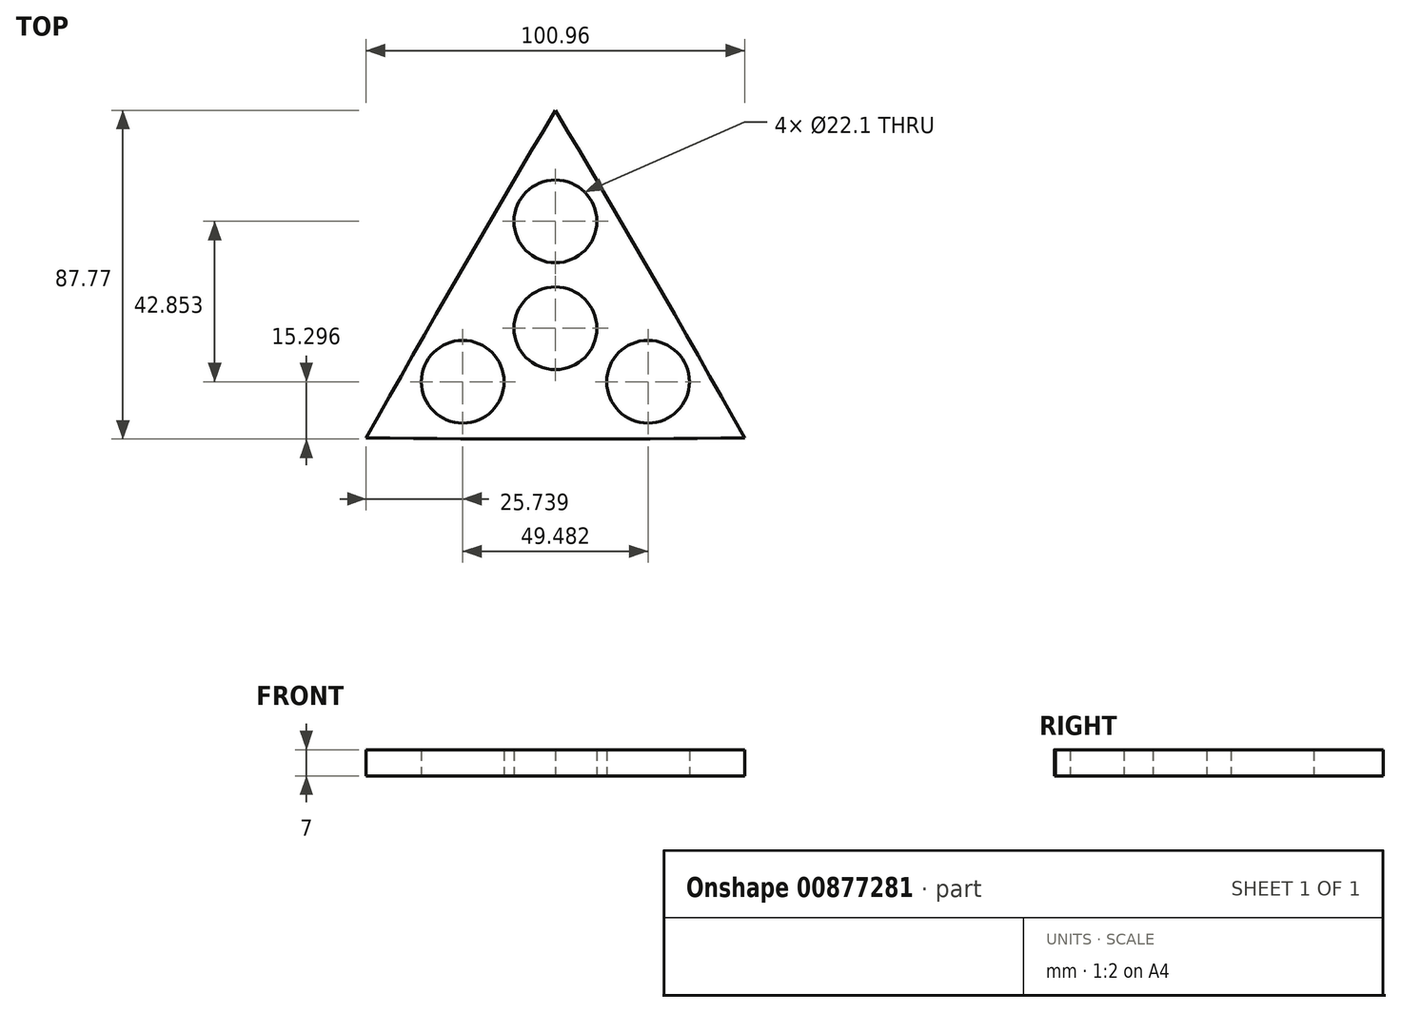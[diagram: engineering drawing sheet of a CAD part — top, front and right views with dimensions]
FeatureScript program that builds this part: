
annotation { "Feature Type Name" : "Feature", "Feature Type Description" : "" }
export const myFeature = defineFeature(function(context is Context, id is Id, definition is map)
    precondition{}
    {
        {
            var Q0;
            Q0=qCreatedBy(makeId("Top.planeOp"),FACE);
            var sketch = newSketch(context, id + "F0", { "sketchPlane" : qUnion([Q0])});
            skCircle(sketch, "E0", {"center": v(0, 0) * mm, "radius": 11.05 * mm});
            skCircle(sketch, "E1", {"center": v(0, 0) * mm, "radius": 13.55 * mm});
            skCircle(sketch, "E2", {"center": v(0, 28.57) * mm, "radius": 11.05 * mm});
            skCircle(sketch, "E3", {"center": v(0, 28.57) * mm, "radius": 13.55 * mm});
            skCircle(sketch, "E4.1.0", {"center": v(-24.74, -14.28) * mm, "radius": 13.55 * mm});
            skCircle(sketch, "E4.1.1", {"center": v(-24.74, -14.28) * mm, "radius": 11.05 * mm});
            skCircle(sketch, "E4.2.0", {"center": v(24.74, -14.28) * mm, "radius": 13.55 * mm});
            skCircle(sketch, "E4.2.1", {"center": v(24.74, -14.28) * mm, "radius": 11.05 * mm});
            skArc(sketch, "E5", {"start": v(0, 58.2) * mm, "mid": v(-25.53, 14.64) * mm, "end": v(-50.48, -29.25) * mm});
            skArc(sketch, "E6.1.0", {"start": v(-50.48, -29.25) * mm, "mid": v(0, -29.58) * mm, "end": v(50.48, -29.25) * mm});
            skArc(sketch, "E6.2.0", {"start": v(50.48, -29.25) * mm, "mid": v(25.53, 14.64) * mm, "end": v(0, 58.2) * mm});
            skPoint(sketch, "E6.center", {"position": v(0, -0.1) * mm});
            skSolve(sketch);
        }
        {
            var Q0;
            Q0 = qSketchRegion(id + "F0", true);
            var Q1;
            Q1=makeQuery(id+"F0.imprint","IMPRINT",FACE,{"disambiguationData":[TD([[makeQuery(id+"F0.imprint","IMPRINT",EDGE,{"derivedFrom":sQuery(id+"F0.wireOp",EDGE,"E0")}),-1.0]])]});
            var Q2;
            Q2=makeQuery(id+"F0.imprint","IMPRINT",FACE,{"disambiguationData":[TD([[makeQuery(id+"F0.imprint","IMPRINT",EDGE,{"derivedFrom":sQuery(id+"F0.wireOp",EDGE,"E4.1.0")}),1.0]])]});
            var Q3;
            Q3=makeQuery(id+"F0.imprint","IMPRINT",FACE,{"disambiguationData":[TD([[makeQuery(id+"F0.imprint","IMPRINT",EDGE,{"derivedFrom":sQuery(id+"F0.wireOp",EDGE,"E2")}),-1.0]])]});
            var Q4;
            Q4=makeQuery(id+"F0.imprint","IMPRINT",FACE,{"disambiguationData":[TD([[makeQuery(id+"F0.imprint","IMPRINT",EDGE,{"derivedFrom":sQuery(id+"F0.wireOp",EDGE,"E4.2.0")}),1.0]])]});
            extrude(context, id + "F1", {"entities" : qUnion([Q0, Q1, Q2, Q3, Q4]), "depth" : 7 * mm, "offsetDistance" : 25 * mm});
        }
    });
